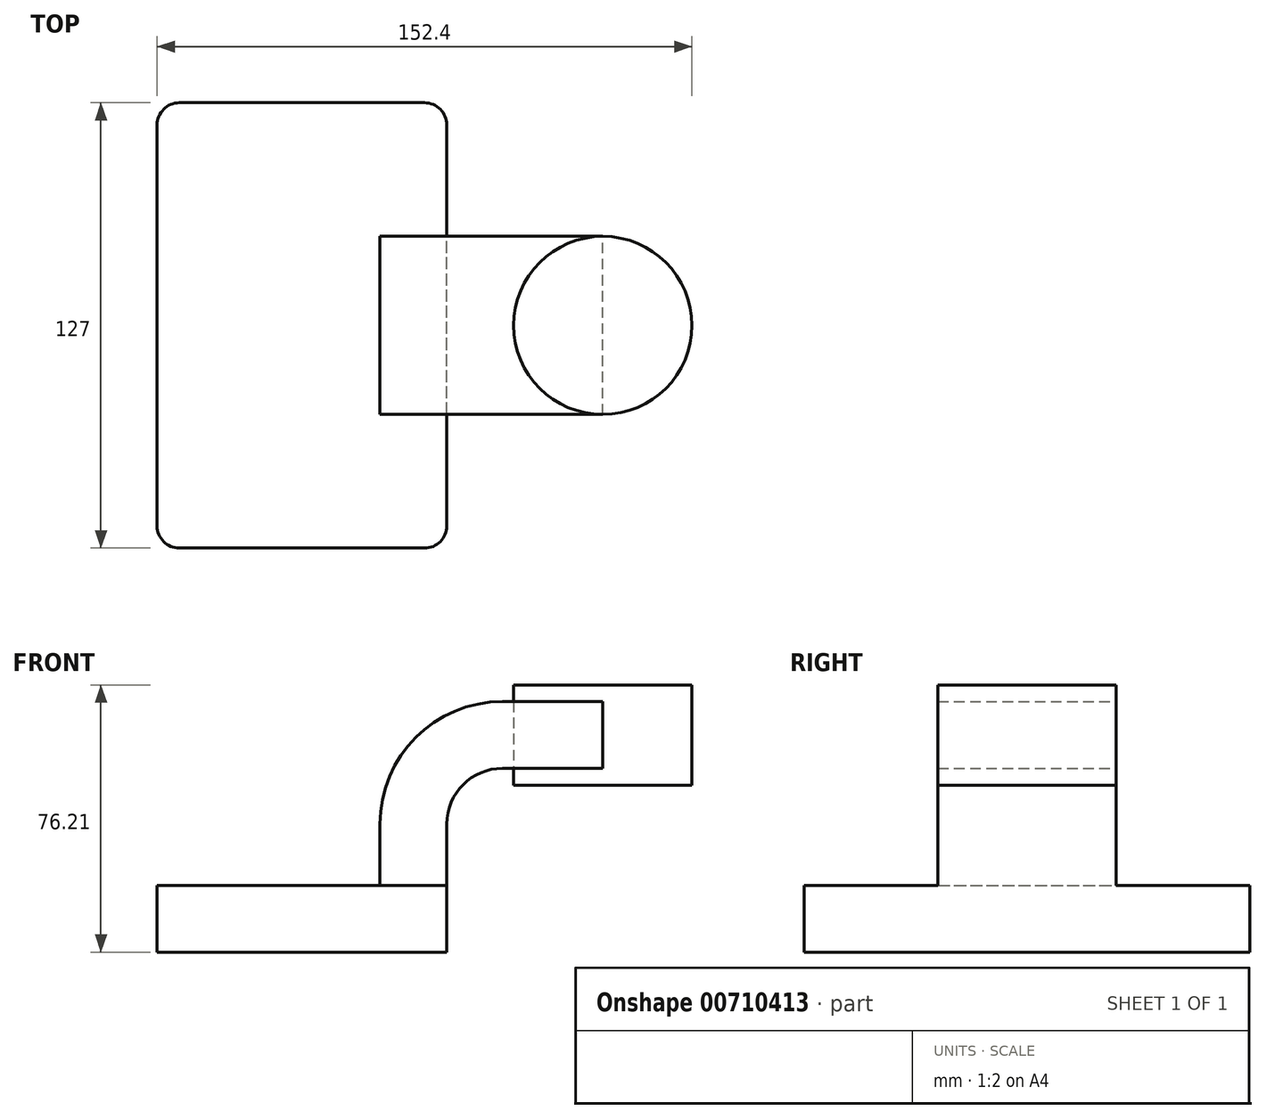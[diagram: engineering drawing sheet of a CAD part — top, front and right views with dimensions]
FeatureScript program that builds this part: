
annotation { "Feature Type Name" : "Feature", "Feature Type Description" : "" }
export const myFeature = defineFeature(function(context is Context, id is Id, definition is map)
    precondition{}
    {
        {
            var Q0;
            Q0=qCreatedBy(makeId("Front.planeOp"),FACE);
            var sketch = newSketch(context, id + "F0", { "sketchPlane" : qUnion([Q0])});
            skLineSegment(sketch, "E0.bottom", {"start": v(33.33, -9.53) * mm, "end": v(-49.22, -9.52) * mm});
            skLineSegment(sketch, "E0.top", {"start": v(33.33, 9.52) * mm, "end": v(-49.22, 9.53) * mm});
            skLineSegment(sketch, "E0.left", {"start": v(33.33, -9.53) * mm, "end": v(33.33, 9.53) * mm});
            skLineSegment(sketch, "E0.right", {"start": v(-49.22, -9.53) * mm, "end": v(-49.22, 9.53) * mm});
            skPoint(sketch, "E0.middle", {"position": v(-7.94, 0) * mm});
            skLineSegment(sketch, "E1.bottom", {"start": v(103.18, 38.1) * mm, "end": v(52.38, 38.1) * mm});
            skLineSegment(sketch, "E1.top", {"start": v(103.18, 66.67) * mm, "end": v(52.38, 66.67) * mm});
            skLineSegment(sketch, "E1.left", {"start": v(103.18, 38.1) * mm, "end": v(103.18, 66.67) * mm});
            skLineSegment(sketch, "E1.right", {"start": v(52.38, 38.1) * mm, "end": v(52.38, 66.67) * mm});
            skPoint(sketch, "E1.middle", {"position": v(77.78, 52.39) * mm});
            skLineSegment(sketch, "E2", {"start": v(33.33, 9.53) * mm, "end": v(33.33, 27) * mm});
            skLineSegment(sketch, "E3", {"start": v(49.2, 42.88) * mm, "end": v(77.78, 42.88) * mm});
            skArc(sketch, "E4", {"start": v(33.33, 27) * mm, "mid": v(37.98, 38.23) * mm, "end": v(49.2, 42.88) * mm});
            skPoint(sketch, "E5", {"position": v(77.78, 38.1) * mm});
            skLineSegment(sketch, "E6.0", {"start": v(49.2, 61.93) * mm, "end": v(84.08, 61.93) * mm});
            skArc(sketch, "E6.1", {"start": v(14.28, 27) * mm, "mid": v(24.51, 51.7) * mm, "end": v(49.2, 61.93) * mm});
            skLineSegment(sketch, "E6.2", {"start": v(14.28, 9.52) * mm, "end": v(14.28, 27) * mm});
            skFitSpline(sketch, "E7", {"points": [v(-49.22, 9.53) * mm, v(49.2, 61.93) * mm], "startDerivative": vector(49.5, 87.6) * mm, "endDerivative": vector(109.05, -10.1) * mm});
            skLineSegment(sketch, "E8", {"start": v(77.78, 38.1) * mm, "end": v(77.78, 66.67) * mm});
            skSolve(sketch);
        }
        {
            var Q0;
            Q0=makeQuery(id+"F0.imprint","IMPRINT",FACE,{"disambiguationData":[TD([[makeQuery(id+"F0.imprint","IMPRINT",EDGE,{"derivedFrom":sQuery(id+"F0.wireOp",EDGE,"E0.bottom")}),-1.0]])]});
            extrude(context, id + "F1", {"entities" : qUnion([Q0]), "endBound" : BoundingType.SYMMETRIC, "depth" : 127 * mm, "offsetDistance" : 25.4 * mm});
        }
        {
            var Q0;
            {var subQ4=sQuery(id+"F0.wireOp",EDGE,"E2");Q0=makeQuery(id+"F0.imprint","IMPRINT",FACE,{"disambiguationData":[TD([[makeQuery(id+"F0.imprint","IMPRINT",EDGE,{"derivedFrom":subQ4}),1.0]])]});}
            var Q1;
            {var subQ0=sQuery(id+"F0.wireOp",EDGE,"E3");var subQ1=sQuery(id+"F0.wireOp",EDGE,"E1.right");var subQ2=makeQuery(id+"F0.imprint","INTERSECT",VERTEX,{"derivedFrom":[subQ1,subQ0]});Q1=makeQuery(id+"F0.imprint","IMPRINT",FACE,{"disambiguationData":[TD([[makeQuery(id+"F0.imprint","IMPRINT",EDGE,{"disambiguationData":[TD([[subQ2,-1.0]])],"derivedFrom":subQ1}),-1.0]])]});}
            extrude(context, id + "F2", {"entities" : qUnion([Q0, Q1]), "operationType" : NewBodyOperationType.ADD, "endBound" : BoundingType.SYMMETRIC, "depth" : 50.8 * mm, "offsetDistance" : 25.4 * mm});
        }
        {
            var Q0;
            Q0=makeQuery(id+"F0.imprint","IMPRINT",FACE,{"disambiguationData":[TD([[makeQuery(id+"F0.imprint","IMPRINT",EDGE,{"derivedFrom":sQuery(id+"F0.wireOp",EDGE,"E6.1")}),1.0]])]});
            extrude(context, id + "F3", {"entities" : qUnion([Q0]), "operationType" : NewBodyOperationType.ADD, "endBound" : BoundingType.SYMMETRIC, "depth" : 15.88 * mm, "offsetDistance" : 25.4 * mm});
        }
        {
            var Q0;
            {var subQ0=sQuery(id+"F0.wireOp",EDGE,"E1.left");Q0=makeQuery(id+"F0.imprint","IMPRINT",FACE,{"disambiguationData":[TD([[makeQuery(id+"F0.imprint","IMPRINT",EDGE,{"derivedFrom":subQ0}),1.0]])]});}
            var Q1;
            Q1=sQuery(id+"F0.wireOp",EDGE,"E8");
            revolve(context, id + "F4", {"entities" : qUnion([Q0]), "axis" : qUnion([Q1]), "revolveType" : RevolveType.FULL});
        }
        {
            var Q0;
            Q0=makeQuery(id+"F1.opExtrude","CAP_EDGE",EDGE,{"disambiguationData":[OSD([sQuery(id+"F0.wireOp",EDGE,"E0.right")])],"isStart":false});
            var Q1;
            Q1=makeQuery(id+"F1.opExtrude","CAP_EDGE",EDGE,{"disambiguationData":[OSD([sQuery(id+"F0.wireOp",EDGE,"E0.left")])],"isStart":false});
            var Q2;
            Q2=makeQuery(id+"F1.opExtrude","CAP_EDGE",EDGE,{"disambiguationData":[OSD([sQuery(id+"F0.wireOp",EDGE,"E0.left")])],"isStart":true});
            var Q3;
            Q3=makeQuery(id+"F1.opExtrude","CAP_EDGE",EDGE,{"disambiguationData":[OSD([sQuery(id+"F0.wireOp",EDGE,"E0.right")])],"isStart":true});
            fillet(context, id + "F5", {"entities" : qUnion([Q0, Q1, Q2, Q3]), "radius" : 6.35 * mm, "tangentPropagation" : true, "allowEdgeOverflow" : false});
        }
    });
